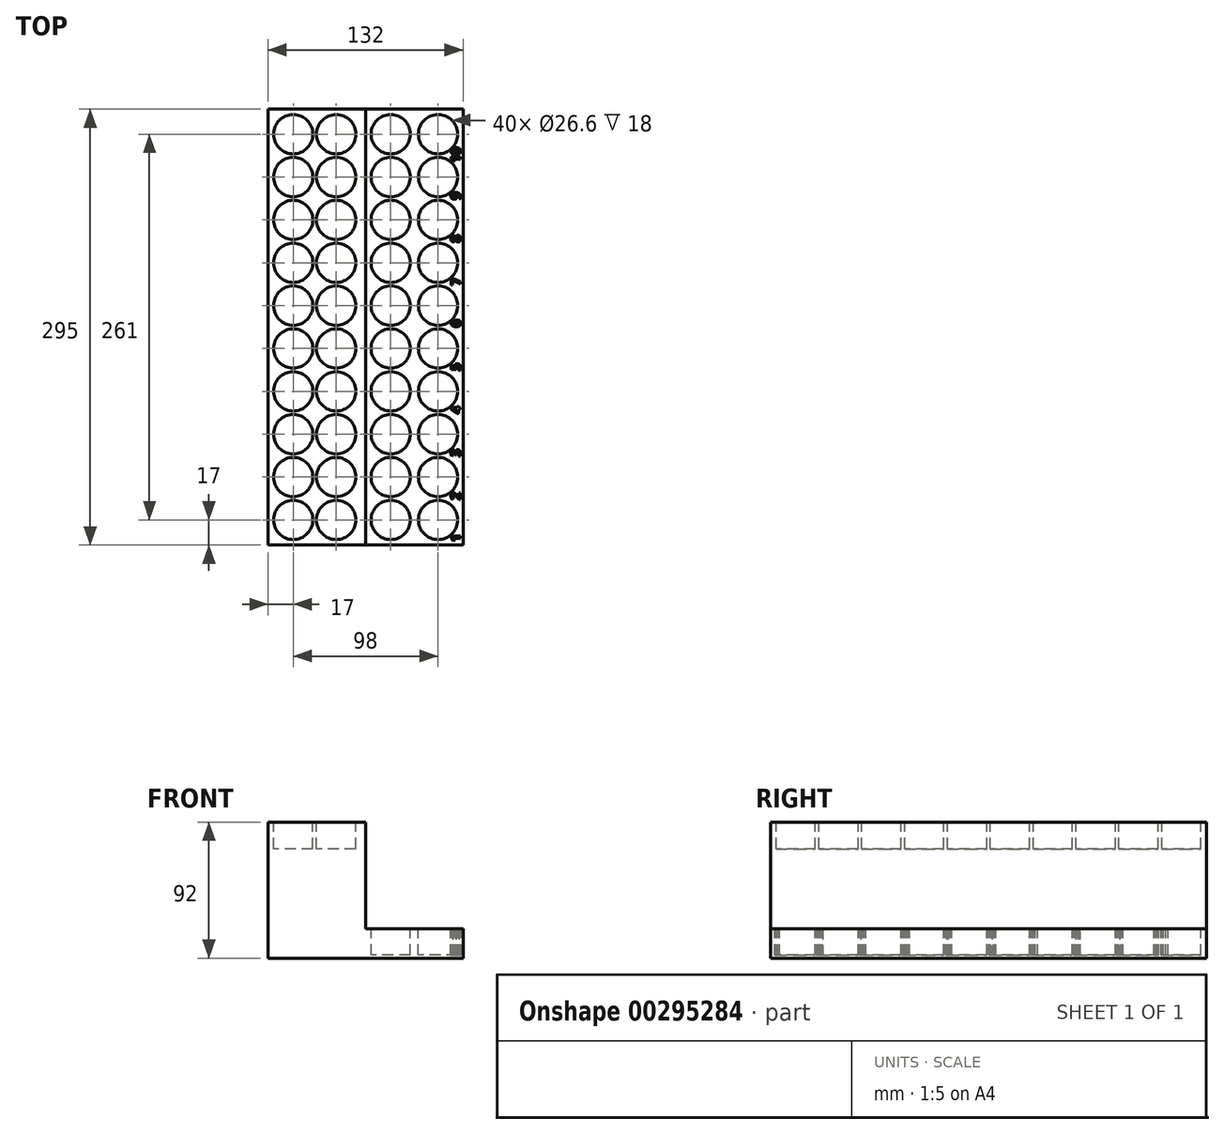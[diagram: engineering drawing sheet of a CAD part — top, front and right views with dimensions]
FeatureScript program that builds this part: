
annotation { "Feature Type Name" : "Feature", "Feature Type Description" : "" }
export const myFeature = defineFeature(function(context is Context, id is Id, definition is map)
    precondition{}
    {
        {
            var Q0;
            Q0=qCreatedBy(makeId("Front.planeOp"),FACE);
            var sketch = newSketch(context, id + "F0", { "sketchPlane" : qUnion([Q0])});
            skLineSegment(sketch, "E0.bottom", {"start": v(-28.8, -20.22) * mm, "end": v(37.2, -20.22) * mm});
            skLineSegment(sketch, "E0.top", {"start": v(-28.8, -40.22) * mm, "end": v(37.2, -40.22) * mm});
            skLineSegment(sketch, "E0.left", {"start": v(-28.8, -20.22) * mm, "end": v(-28.8, -40.22) * mm});
            skLineSegment(sketch, "E0.right", {"start": v(37.2, -20.22) * mm, "end": v(37.2, -40.22) * mm});
            skSolve(sketch);
        }
        {
            var Q0;
            Q0 = qSketchRegion(id + "F0", true);
            extrude(context, id + "F1", {"entities" : qUnion([Q0]), "oppositeDirection" : true, "depth" : 295 * mm});
        }
        {
            var Q0;
            Q0=makeQuery(id+"F1.opExtrude","SWEPT_FACE",FACE,{"disambiguationData":[OSD([sQuery(id+"F0.wireOp",EDGE,"E0.bottom")])]});
            var sketch = newSketch(context, id + "F2", { "sketchPlane" : qUnion([Q0])});
            skCircle(sketch, "E1", {"center": v(-11.8, 17) * mm, "radius": 13.3 * mm});
            skCircle(sketch, "E2", {"center": v(20.2, 17) * mm, "radius": 13.3 * mm});
            skCircle(sketch, "E3", {"center": v(-11.8, 46) * mm, "radius": 13.3 * mm});
            skCircle(sketch, "E4", {"center": v(20.2, 46) * mm, "radius": 13.3 * mm});
            skCircle(sketch, "E5", {"center": v(-11.8, 75) * mm, "radius": 13.3 * mm});
            skCircle(sketch, "E6", {"center": v(20.2, 75) * mm, "radius": 13.3 * mm});
            skCircle(sketch, "E7", {"center": v(-11.8, 104) * mm, "radius": 13.3 * mm});
            skCircle(sketch, "E8", {"center": v(20.2, 104) * mm, "radius": 13.3 * mm});
            skCircle(sketch, "E9", {"center": v(-11.8, 133) * mm, "radius": 13.3 * mm});
            skCircle(sketch, "E10", {"center": v(20.2, 133) * mm, "radius": 13.3 * mm});
            skCircle(sketch, "E11", {"center": v(-11.8, 162) * mm, "radius": 13.3 * mm});
            skCircle(sketch, "E12", {"center": v(20.2, 162) * mm, "radius": 13.3 * mm});
            skCircle(sketch, "E13", {"center": v(-11.8, 191) * mm, "radius": 13.3 * mm});
            skCircle(sketch, "E14", {"center": v(20.2, 191) * mm, "radius": 13.3 * mm});
            skCircle(sketch, "E15", {"center": v(-11.8, 220) * mm, "radius": 13.3 * mm});
            skCircle(sketch, "E16", {"center": v(20.2, 220) * mm, "radius": 13.3 * mm});
            skCircle(sketch, "E17", {"center": v(-11.8, 249) * mm, "radius": 13.3 * mm});
            skCircle(sketch, "E18", {"center": v(20.2, 249) * mm, "radius": 13.3 * mm});
            skCircle(sketch, "E19", {"center": v(-11.8, 278) * mm, "radius": 13.3 * mm});
            skCircle(sketch, "E20", {"center": v(20.2, 278) * mm, "radius": 13.3 * mm});
            skText(sketch, "E21", { "text": "1", "fontName": "OpenSans-Bold.ttf"});
            skText(sketch, "E22", { "text": "4", "fontName": "OpenSans-Bold.ttf"});
            skText(sketch, "E23", { "text": "3", "fontName": "OpenSans-Bold.ttf"});
            skText(sketch, "E24", { "text": "2\n", "fontName": "OpenSans-Bold.ttf"});
            skText(sketch, "E25", { "text": "5\n", "fontName": "OpenSans-Bold.ttf"});
            skText(sketch, "E26", { "text": "6", "fontName": "OpenSans-Bold.ttf"});
            skText(sketch, "E27", { "text": "7", "fontName": "OpenSans-Bold.ttf"});
            skText(sketch, "E28", { "text": "8", "fontName": "OpenSans-Bold.ttf"});
            skText(sketch, "E29", { "text": "9", "fontName": "OpenSans-Bold.ttf"});
            skText(sketch, "E30", { "text": "10", "fontName": "OpenSans-Bold.ttf"});
            const initialGuessF2  = {"E21": [0.03547, 0.00224, 0, 1, 0.00658], "E22": [0.03547, 0.0888, 0, 1, 0.00658], "E23": [0.03547, 0.05971, 0, 1, 0.00658], "E24": [0.03547, 0.0305, 0, 1, 0.00658], "E25": [0.03547, 0.1179, 0, 1, 0.00658], "E26": [0.03547, 0.1474, 0, 1, 0.00658], "E27": [0.03547, 0.17573, 0, 1, 0.00658], "E28": [0.03547, 0.20472, 0, 1, 0.00658], "E29": [0.03547, 0.23372, 0, 1, 0.00658], "E30": [0.03547, 0.2588, 0, 1, 0.00658]};
            skSetInitialGuess(sketch, initialGuessF2);
            skSolve(sketch);
        }
        {
            var Q0;
            Q0=makeQuery(id+"F2.imprint","IMPRINT",FACE,{"disambiguationData":[TD([[makeQuery(id+"F2.imprint","IMPRINT",EDGE,{"derivedFrom":sQuery(id+"F2.wireOp",EDGE,"E1")}),1.0]])]});
            var Q1;
            Q1=makeQuery(id+"F2.imprint","IMPRINT",FACE,{"disambiguationData":[TD([[makeQuery(id+"F2.imprint","IMPRINT",EDGE,{"derivedFrom":sQuery(id+"F2.wireOp",EDGE,"E3")}),1.0]])]});
            var Q2;
            Q2=makeQuery(id+"F2.imprint","IMPRINT",FACE,{"disambiguationData":[TD([[makeQuery(id+"F2.imprint","IMPRINT",EDGE,{"derivedFrom":sQuery(id+"F2.wireOp",EDGE,"E5")}),1.0]])]});
            var Q3;
            Q3=makeQuery(id+"F2.imprint","IMPRINT",FACE,{"disambiguationData":[TD([[makeQuery(id+"F2.imprint","IMPRINT",EDGE,{"derivedFrom":sQuery(id+"F2.wireOp",EDGE,"E7")}),1.0]])]});
            var Q4;
            Q4=makeQuery(id+"F2.imprint","IMPRINT",FACE,{"disambiguationData":[TD([[makeQuery(id+"F2.imprint","IMPRINT",EDGE,{"derivedFrom":sQuery(id+"F2.wireOp",EDGE,"E9")}),1.0]])]});
            var Q5;
            Q5=makeQuery(id+"F2.imprint","IMPRINT",FACE,{"disambiguationData":[TD([[makeQuery(id+"F2.imprint","IMPRINT",EDGE,{"derivedFrom":sQuery(id+"F2.wireOp",EDGE,"E11")}),1.0]])]});
            var Q6;
            Q6=makeQuery(id+"F2.imprint","IMPRINT",FACE,{"disambiguationData":[TD([[makeQuery(id+"F2.imprint","IMPRINT",EDGE,{"derivedFrom":sQuery(id+"F2.wireOp",EDGE,"E13")}),1.0]])]});
            var Q7;
            Q7=makeQuery(id+"F2.imprint","IMPRINT",FACE,{"disambiguationData":[TD([[makeQuery(id+"F2.imprint","IMPRINT",EDGE,{"derivedFrom":sQuery(id+"F2.wireOp",EDGE,"E15")}),1.0]])]});
            var Q8;
            Q8=makeQuery(id+"F2.imprint","IMPRINT",FACE,{"disambiguationData":[TD([[makeQuery(id+"F2.imprint","IMPRINT",EDGE,{"derivedFrom":sQuery(id+"F2.wireOp",EDGE,"E17")}),1.0]])]});
            var Q9;
            Q9=makeQuery(id+"F2.imprint","IMPRINT",FACE,{"disambiguationData":[TD([[makeQuery(id+"F2.imprint","IMPRINT",EDGE,{"derivedFrom":sQuery(id+"F2.wireOp",EDGE,"E19")}),1.0]])]});
            var Q10;
            Q10=makeQuery(id+"F2.imprint","IMPRINT",FACE,{"disambiguationData":[TD([[makeQuery(id+"F2.imprint","IMPRINT",EDGE,{"derivedFrom":sQuery(id+"F2.wireOp",EDGE,"E20")}),1.0]])]});
            var Q11;
            Q11=makeQuery(id+"F2.imprint","IMPRINT",FACE,{"disambiguationData":[TD([[makeQuery(id+"F2.imprint","IMPRINT",EDGE,{"derivedFrom":sQuery(id+"F2.wireOp",EDGE,"E18")}),1.0]])]});
            var Q12;
            Q12=makeQuery(id+"F2.imprint","IMPRINT",FACE,{"disambiguationData":[TD([[makeQuery(id+"F2.imprint","IMPRINT",EDGE,{"derivedFrom":sQuery(id+"F2.wireOp",EDGE,"E16")}),1.0]])]});
            var Q13;
            Q13=makeQuery(id+"F2.imprint","IMPRINT",FACE,{"disambiguationData":[TD([[makeQuery(id+"F2.imprint","IMPRINT",EDGE,{"derivedFrom":sQuery(id+"F2.wireOp",EDGE,"E14")}),1.0]])]});
            var Q14;
            Q14=makeQuery(id+"F2.imprint","IMPRINT",FACE,{"disambiguationData":[TD([[makeQuery(id+"F2.imprint","IMPRINT",EDGE,{"derivedFrom":sQuery(id+"F2.wireOp",EDGE,"E12")}),1.0]])]});
            var Q15;
            Q15=makeQuery(id+"F2.imprint","IMPRINT",FACE,{"disambiguationData":[TD([[makeQuery(id+"F2.imprint","IMPRINT",EDGE,{"derivedFrom":sQuery(id+"F2.wireOp",EDGE,"E10")}),1.0]])]});
            var Q16;
            Q16=makeQuery(id+"F2.imprint","IMPRINT",FACE,{"disambiguationData":[TD([[makeQuery(id+"F2.imprint","IMPRINT",EDGE,{"derivedFrom":sQuery(id+"F2.wireOp",EDGE,"E8")}),1.0]])]});
            var Q17;
            Q17=makeQuery(id+"F2.imprint","IMPRINT",FACE,{"disambiguationData":[TD([[makeQuery(id+"F2.imprint","IMPRINT",EDGE,{"derivedFrom":sQuery(id+"F2.wireOp",EDGE,"E6")}),1.0]])]});
            var Q18;
            Q18=makeQuery(id+"F2.imprint","IMPRINT",FACE,{"disambiguationData":[TD([[makeQuery(id+"F2.imprint","IMPRINT",EDGE,{"derivedFrom":sQuery(id+"F2.wireOp",EDGE,"E4")}),1.0]])]});
            var Q19;
            Q19=makeQuery(id+"F2.imprint","IMPRINT",FACE,{"disambiguationData":[TD([[makeQuery(id+"F2.imprint","IMPRINT",EDGE,{"derivedFrom":sQuery(id+"F2.wireOp",EDGE,"E2")}),1.0]])]});
            var Q20;
            Q20=sQuery(id+"F2.wireOp",EDGE,"E1");
            var Q21;
            Q21=sQuery(id+"F2.wireOp",EDGE,"E2");
            extrude(context, id + "F3", {"entities" : qUnion([Q0, Q1, Q2, Q3, Q4, Q5, Q6, Q7, Q8, Q9, Q10, Q11, Q12, Q13, Q14, Q15, Q16, Q17, Q18, Q19]), "operationType" : NewBodyOperationType.REMOVE, "surfaceEntities" : qUnion([Q20, Q21]), "oppositeDirection" : true, "depth" : 18 * mm});
        }
        {
            var Q0;
            Q0=makeQuery(id+"F1.opExtrude","CAP_FACE",FACE,{"disambiguationData":[OSD([sQuery(id+"F0.wireOp",EDGE,"E0.bottom"),sQuery(id+"F0.wireOp",EDGE,"E0.top"),sQuery(id+"F0.wireOp",EDGE,"E0.left"),sQuery(id+"F0.wireOp",EDGE,"E0.right")])],"isStart":true});
            var sketch = newSketch(context, id + "F4", { "sketchPlane" : qUnion([Q0])});
            skLineSegment(sketch, "E31.0", {"start": v(-28.8, -20.22) * mm, "end": v(-28.8, -40.22) * mm});
            skLineSegment(sketch, "E32", {"start": v(-28.8, -40.22) * mm, "end": v(-94.8, -40.22) * mm});
            skLineSegment(sketch, "E33", {"start": v(-94.8, -40.22) * mm, "end": v(-94.8, 51.78) * mm});
            skLineSegment(sketch, "E34", {"start": v(-94.8, 51.78) * mm, "end": v(-28.8, 51.78) * mm});
            skLineSegment(sketch, "E35", {"start": v(-28.8, 51.78) * mm, "end": v(-28.8, -20.22) * mm});
            skSolve(sketch);
        }
        {
            var Q0;
            Q0=makeQuery(id+"F4.imprint","IMPRINT",FACE,{"disambiguationData":[TD([[makeQuery(id+"F4.imprint","IMPRINT",EDGE,{"derivedFrom":sQuery(id+"F4.wireOp",EDGE,"E31.0")}),-1.0]])]});
            extrude(context, id + "F5", {"entities" : qUnion([Q0]), "operationType" : NewBodyOperationType.ADD, "oppositeDirection" : true, "depth" : 295 * mm});
        }
        {
            var Q0;
            Q0=makeQuery(id+"F5.opExtrude","SWEPT_FACE",FACE,{"disambiguationData":[OSD([sQuery(id+"F4.wireOp",EDGE,"E34")])]});
            var sketch = newSketch(context, id + "F6", { "sketchPlane" : qUnion([Q0])});
            skCircle(sketch, "E36", {"center": v(-77.8, 17) * mm, "radius": 13.3 * mm});
            skCircle(sketch, "E37", {"center": v(-48.69, 17) * mm, "radius": 13.3 * mm});
            skCircle(sketch, "E38", {"center": v(-77.8, 46) * mm, "radius": 13.3 * mm});
            skCircle(sketch, "E39", {"center": v(-48.69, 46) * mm, "radius": 13.3 * mm});
            skCircle(sketch, "E40", {"center": v(-77.8, 75) * mm, "radius": 13.3 * mm});
            skCircle(sketch, "E41", {"center": v(-48.69, 75) * mm, "radius": 13.3 * mm});
            skCircle(sketch, "E42", {"center": v(-77.8, 104) * mm, "radius": 13.3 * mm});
            skCircle(sketch, "E43", {"center": v(-48.69, 104) * mm, "radius": 13.3 * mm});
            skCircle(sketch, "E44", {"center": v(-77.8, 133) * mm, "radius": 13.3 * mm});
            skCircle(sketch, "E45", {"center": v(-48.69, 133) * mm, "radius": 13.3 * mm});
            skCircle(sketch, "E46", {"center": v(-77.8, 162) * mm, "radius": 13.3 * mm});
            skCircle(sketch, "E47", {"center": v(-48.69, 162) * mm, "radius": 13.3 * mm});
            skCircle(sketch, "E48", {"center": v(-77.8, 191) * mm, "radius": 13.3 * mm});
            skCircle(sketch, "E49", {"center": v(-48.69, 191) * mm, "radius": 13.3 * mm});
            skCircle(sketch, "E50", {"center": v(-77.8, 220) * mm, "radius": 13.3 * mm});
            skCircle(sketch, "E51", {"center": v(-48.69, 220) * mm, "radius": 13.3 * mm});
            skCircle(sketch, "E52", {"center": v(-77.8, 249) * mm, "radius": 13.3 * mm});
            skCircle(sketch, "E53", {"center": v(-48.69, 249) * mm, "radius": 13.3 * mm});
            skCircle(sketch, "E54", {"center": v(-77.8, 278) * mm, "radius": 13.3 * mm});
            skCircle(sketch, "E55", {"center": v(-48.69, 278) * mm, "radius": 13.3 * mm});
            skSolve(sketch);
        }
        {
            var Q0;
            Q0=makeQuery(id+"F6.imprint","IMPRINT",FACE,{"disambiguationData":[TD([[makeQuery(id+"F6.imprint","IMPRINT",EDGE,{"derivedFrom":sQuery(id+"F6.wireOp",EDGE,"E36")}),1.0]])]});
            var Q1;
            Q1=makeQuery(id+"F6.imprint","IMPRINT",FACE,{"disambiguationData":[TD([[makeQuery(id+"F6.imprint","IMPRINT",EDGE,{"derivedFrom":sQuery(id+"F6.wireOp",EDGE,"E37")}),1.0]])]});
            var Q2;
            Q2=makeQuery(id+"F6.imprint","IMPRINT",FACE,{"disambiguationData":[TD([[makeQuery(id+"F6.imprint","IMPRINT",EDGE,{"derivedFrom":sQuery(id+"F6.wireOp",EDGE,"E38")}),1.0]])]});
            var Q3;
            Q3=makeQuery(id+"F6.imprint","IMPRINT",FACE,{"disambiguationData":[TD([[makeQuery(id+"F6.imprint","IMPRINT",EDGE,{"derivedFrom":sQuery(id+"F6.wireOp",EDGE,"E39")}),1.0]])]});
            var Q4;
            Q4=makeQuery(id+"F6.imprint","IMPRINT",FACE,{"disambiguationData":[TD([[makeQuery(id+"F6.imprint","IMPRINT",EDGE,{"derivedFrom":sQuery(id+"F6.wireOp",EDGE,"E41")}),1.0]])]});
            var Q5;
            Q5=makeQuery(id+"F6.imprint","IMPRINT",FACE,{"disambiguationData":[TD([[makeQuery(id+"F6.imprint","IMPRINT",EDGE,{"derivedFrom":sQuery(id+"F6.wireOp",EDGE,"E40")}),1.0]])]});
            var Q6;
            Q6=makeQuery(id+"F6.imprint","IMPRINT",FACE,{"disambiguationData":[TD([[makeQuery(id+"F6.imprint","IMPRINT",EDGE,{"derivedFrom":sQuery(id+"F6.wireOp",EDGE,"E43")}),1.0]])]});
            var Q7;
            Q7=makeQuery(id+"F6.imprint","IMPRINT",FACE,{"disambiguationData":[TD([[makeQuery(id+"F6.imprint","IMPRINT",EDGE,{"derivedFrom":sQuery(id+"F6.wireOp",EDGE,"E42")}),1.0]])]});
            var Q8;
            Q8=makeQuery(id+"F6.imprint","IMPRINT",FACE,{"disambiguationData":[TD([[makeQuery(id+"F6.imprint","IMPRINT",EDGE,{"derivedFrom":sQuery(id+"F6.wireOp",EDGE,"E45")}),1.0]])]});
            var Q9;
            Q9=makeQuery(id+"F6.imprint","IMPRINT",FACE,{"disambiguationData":[TD([[makeQuery(id+"F6.imprint","IMPRINT",EDGE,{"derivedFrom":sQuery(id+"F6.wireOp",EDGE,"E44")}),1.0]])]});
            var Q10;
            Q10=makeQuery(id+"F6.imprint","IMPRINT",FACE,{"disambiguationData":[TD([[makeQuery(id+"F6.imprint","IMPRINT",EDGE,{"derivedFrom":sQuery(id+"F6.wireOp",EDGE,"E47")}),1.0]])]});
            var Q11;
            Q11=makeQuery(id+"F6.imprint","IMPRINT",FACE,{"disambiguationData":[TD([[makeQuery(id+"F6.imprint","IMPRINT",EDGE,{"derivedFrom":sQuery(id+"F6.wireOp",EDGE,"E46")}),1.0]])]});
            var Q12;
            Q12=makeQuery(id+"F6.imprint","IMPRINT",FACE,{"disambiguationData":[TD([[makeQuery(id+"F6.imprint","IMPRINT",EDGE,{"derivedFrom":sQuery(id+"F6.wireOp",EDGE,"E49")}),1.0]])]});
            var Q13;
            Q13=makeQuery(id+"F6.imprint","IMPRINT",FACE,{"disambiguationData":[TD([[makeQuery(id+"F6.imprint","IMPRINT",EDGE,{"derivedFrom":sQuery(id+"F6.wireOp",EDGE,"E48")}),1.0]])]});
            var Q14;
            Q14=makeQuery(id+"F6.imprint","IMPRINT",FACE,{"disambiguationData":[TD([[makeQuery(id+"F6.imprint","IMPRINT",EDGE,{"derivedFrom":sQuery(id+"F6.wireOp",EDGE,"E51")}),1.0]])]});
            var Q15;
            Q15=makeQuery(id+"F6.imprint","IMPRINT",FACE,{"disambiguationData":[TD([[makeQuery(id+"F6.imprint","IMPRINT",EDGE,{"derivedFrom":sQuery(id+"F6.wireOp",EDGE,"E50")}),1.0]])]});
            var Q16;
            Q16=makeQuery(id+"F6.imprint","IMPRINT",FACE,{"disambiguationData":[TD([[makeQuery(id+"F6.imprint","IMPRINT",EDGE,{"derivedFrom":sQuery(id+"F6.wireOp",EDGE,"E53")}),1.0]])]});
            var Q17;
            Q17=makeQuery(id+"F6.imprint","IMPRINT",FACE,{"disambiguationData":[TD([[makeQuery(id+"F6.imprint","IMPRINT",EDGE,{"derivedFrom":sQuery(id+"F6.wireOp",EDGE,"E52")}),1.0]])]});
            var Q18;
            Q18=makeQuery(id+"F6.imprint","IMPRINT",FACE,{"disambiguationData":[TD([[makeQuery(id+"F6.imprint","IMPRINT",EDGE,{"derivedFrom":sQuery(id+"F6.wireOp",EDGE,"E55")}),1.0]])]});
            var Q19;
            Q19=makeQuery(id+"F6.imprint","IMPRINT",FACE,{"disambiguationData":[TD([[makeQuery(id+"F6.imprint","IMPRINT",EDGE,{"derivedFrom":sQuery(id+"F6.wireOp",EDGE,"E54")}),1.0]])]});
            var Q20;
            Q20=sQuery(id+"F6.wireOp",EDGE,"E36");
            var Q21;
            Q21=sQuery(id+"F6.wireOp",EDGE,"E37");
            var Q22;
            Q22=sQuery(id+"F6.wireOp",EDGE,"E38");
            var Q23;
            Q23=sQuery(id+"F6.wireOp",EDGE,"E39");
            extrude(context, id + "F7", {"entities" : qUnion([Q0, Q1, Q2, Q3, Q4, Q5, Q6, Q7, Q8, Q9, Q10, Q11, Q12, Q13, Q14, Q15, Q16, Q17, Q18, Q19]), "operationType" : NewBodyOperationType.REMOVE, "surfaceEntities" : qUnion([Q20, Q21, Q22, Q23]), "oppositeDirection" : true, "depth" : 18 * mm});
        }
        {
            var Q0;
            Q0 = qSketchRegion(id + "F2", true);
            extrude(context, id + "F8", {"entities" : qUnion([Q0]), "operationType" : NewBodyOperationType.REMOVE, "oppositeDirection" : true, "depth" : 18 * mm});
        }
    });
